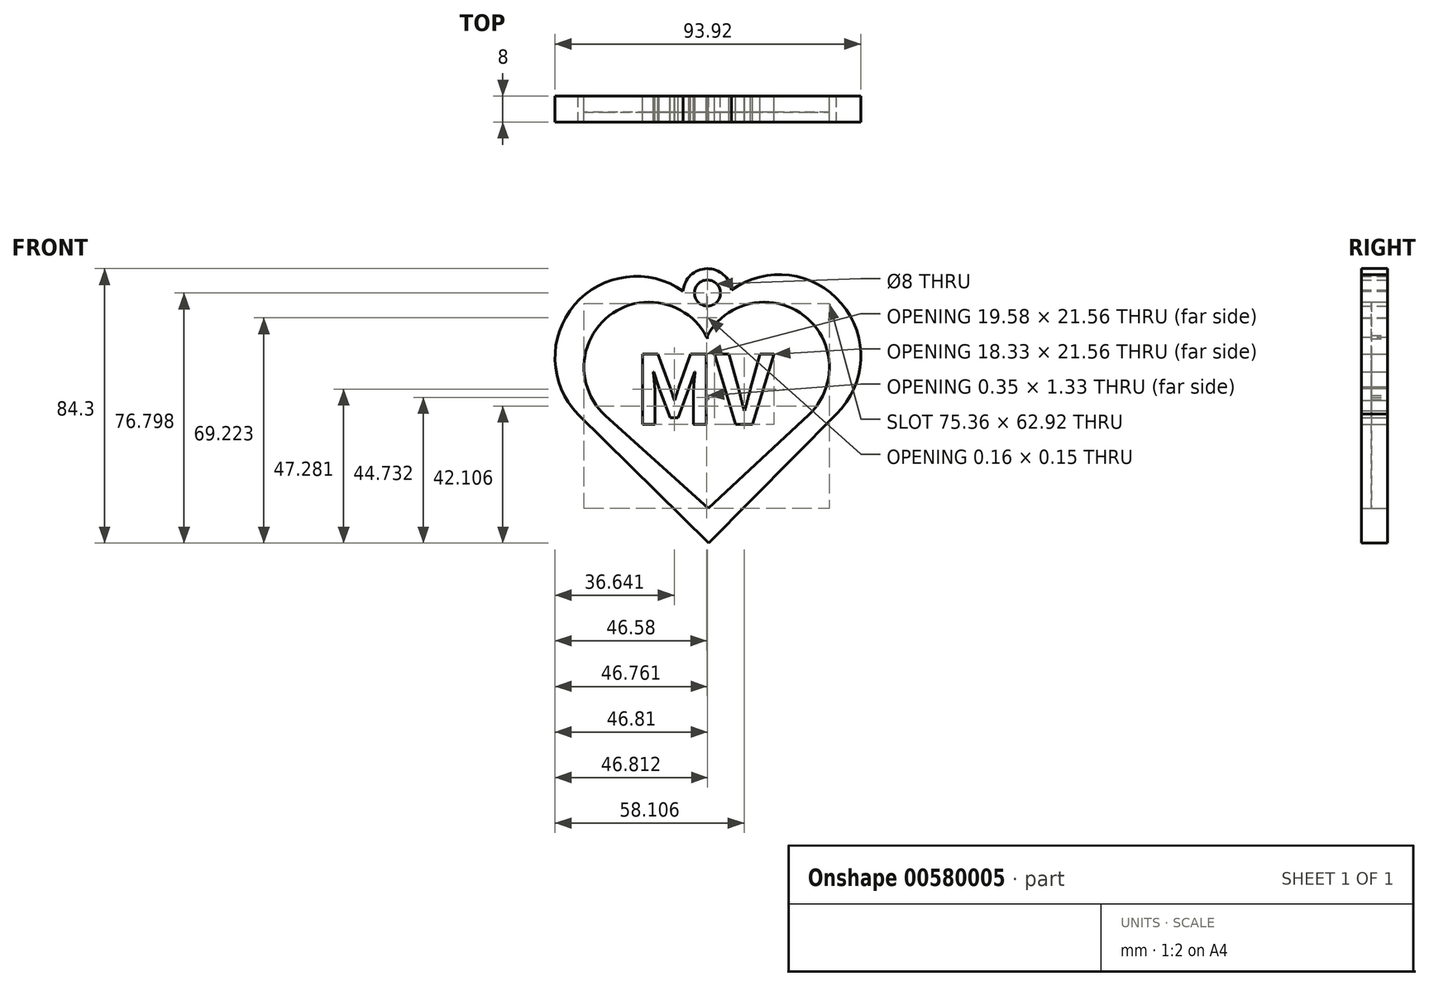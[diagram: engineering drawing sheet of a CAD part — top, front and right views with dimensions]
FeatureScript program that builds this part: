
annotation { "Feature Type Name" : "Feature", "Feature Type Description" : "" }
export const myFeature = defineFeature(function(context is Context, id is Id, definition is map)
    precondition{}
    {
        {
            var Q0;
            Q0=qCreatedBy(makeId("Front.planeOp"),FACE);
            var sketch = newSketch(context, id + "F0", { "sketchPlane" : qUnion([Q0])});
            skArc(sketch, "E0", {"start": v(10.73, 15.13) * mm, "mid": v(10.7, 15.2) * mm, "end": v(10.65, 15.28) * mm});
            skLineSegment(sketch, "E1", {"start": v(11.08, -54.02) * mm, "end": v(-29.06, -14.45) * mm});
            skLineSegment(sketch, "E2", {"start": v(-29.06, -14.45) * mm, "end": v(11.08, -54.02) * mm});
            skLineSegment(sketch, "E3", {"start": v(11.08, -54.02) * mm, "end": v(50.35, -14.38) * mm});
            skPoint(sketch, "E4.orphan", {"position": v(6.42, 2.91) * mm});
            skArc(sketch, "E5.trimOffspring", {"start": v(50.35, -14.38) * mm, "mid": v(51.94, 19.6) * mm, "end": v(18.17, 23.7) * mm});
            skPoint(sketch, "E6.center.orphan", {"position": v(23.92, 2.91) * mm});
            skArc(sketch, "E7", {"start": v(10.76, 8.8) * mm, "mid": v(-19.24, 15.97) * mm, "end": v(-20.6, -14.85) * mm});
            skArc(sketch, "E8", {"start": v(10.5, -9.31) * mm, "mid": v(10.68, -9.63) * mm, "end": v(10.86, -9.95) * mm});
            skLineSegment(sketch, "E9", {"start": v(12.8, 0) * mm, "end": v(8.2, 0) * mm});
            skLineSegment(sketch, "E10", {"start": v(10.76, 9.78) * mm, "end": v(10.76, 8.8) * mm});
            skLineSegment(sketch, "E11", {"start": v(-20.6, -14.85) * mm, "end": v(11.02, -43.38) * mm});
            skLineSegment(sketch, "E12", {"start": v(11.02, -43.38) * mm, "end": v(41.85, -14.63) * mm});
            skLineSegment(sketch, "E13.trimOffspring", {"start": v(-7.2, 0) * mm, "end": v(-8.68, 0) * mm});
            skLineSegment(sketch, "E14.trimOffspring", {"start": v(10.85, -8.62) * mm, "end": v(10.86, -9.95) * mm});
            skArc(sketch, "E15.trimOffspring", {"start": v(41.85, -14.63) * mm, "mid": v(40.34, 15.9) * mm, "end": v(10.5, 9.31) * mm});
            skArc(sketch, "E16.trimOffspring", {"start": v(10.5, -9.31) * mm, "mid": v(10.68, -8.97) * mm, "end": v(10.85, -8.62) * mm});
            skText(sketch, "E17", { "text": "MV", "fontName": "NotoSansCJKkr-Bold.otf"});
            skCircle(sketch, "E18", {"center": v(10.73, 22.78) * mm, "radius": 7.5 * mm});
            skLineSegment(sketch, "E19", {"start": v(10.73, 15.28) * mm, "end": v(10.73, 15.13) * mm});
            skCircle(sketch, "E20", {"center": v(10.73, 22.78) * mm, "radius": 4 * mm});
            skArc(sketch, "E21.trimOffspring", {"start": v(10.81, 15.28) * mm, "mid": v(10.77, 15.2) * mm, "end": v(10.73, 15.13) * mm});
            skArc(sketch, "E22.trimOffspring", {"start": v(3.26, 23.4) * mm, "mid": v(-30.1, 19.15) * mm, "end": v(-29.06, -14.45) * mm});
            const initialGuessF0  = {"E17": [-0.01188, -0.01752, 1, 0, 0.02098]};
            skSetInitialGuess(sketch, initialGuessF0);
            skSolve(sketch);
        }
        {
            var Q0;
            {var subQ1=sQuery(id+"F0.wireOp",EDGE,"E0");Q0=makeQuery(id+"F0.imprint","IMPRINT",FACE,{"disambiguationData":[TD([[makeQuery(id+"F0.imprint","IMPRINT",EDGE,{"derivedFrom":subQ1}),1.0]])]});}
            var Q1;
            Q1=makeQuery(id+"F0.imprint","IMPRINT",FACE,{"disambiguationData":[TD([[makeQuery(id+"F0.imprint","IMPRINT",EDGE,{"derivedFrom":sQuery(id+"F0.wireOp",EDGE,"E17.sketch_text.stroke-0")}),1.0]])]});
            var Q2;
            Q2=makeQuery(id+"F0.imprint","IMPRINT",FACE,{"disambiguationData":[TD([[makeQuery(id+"F0.imprint","IMPRINT",EDGE,{"derivedFrom":sQuery(id+"F0.wireOp",EDGE,"E17.sketch_text.stroke-22")}),1.0]])]});
            extrude(context, id + "F1", {"entities" : qUnion([Q0, Q1, Q2]), "depth" : 8 * mm, "offsetDistance" : 25 * mm});
        }
        {
            var Q0;
            Q0=makeQuery(id+"F0.imprint","IMPRINT",FACE,{"disambiguationData":[TD([[makeQuery(id+"F0.imprint","IMPRINT",EDGE,{"derivedFrom":sQuery(id+"F0.wireOp",EDGE,"E20")}),-1.0]])]});
            extrude(context, id + "F2", {"entities" : qUnion([Q0]), "operationType" : NewBodyOperationType.ADD, "depth" : 8 * mm, "offsetDistance" : 25 * mm});
        }
        {
            var Q0;
            Q0=makeQuery(id+"F0.imprint","IMPRINT",FACE,{"disambiguationData":[TD([[makeQuery(id+"F0.imprint","IMPRINT",EDGE,{"derivedFrom":sQuery(id+"F0.wireOp",EDGE,"E8")}),-1.0]])]});
            extrude(context, id + "F3", {"entities" : qUnion([Q0]), "depth" : 5 * mm, "offsetDistance" : 25 * mm});
        }
    });
